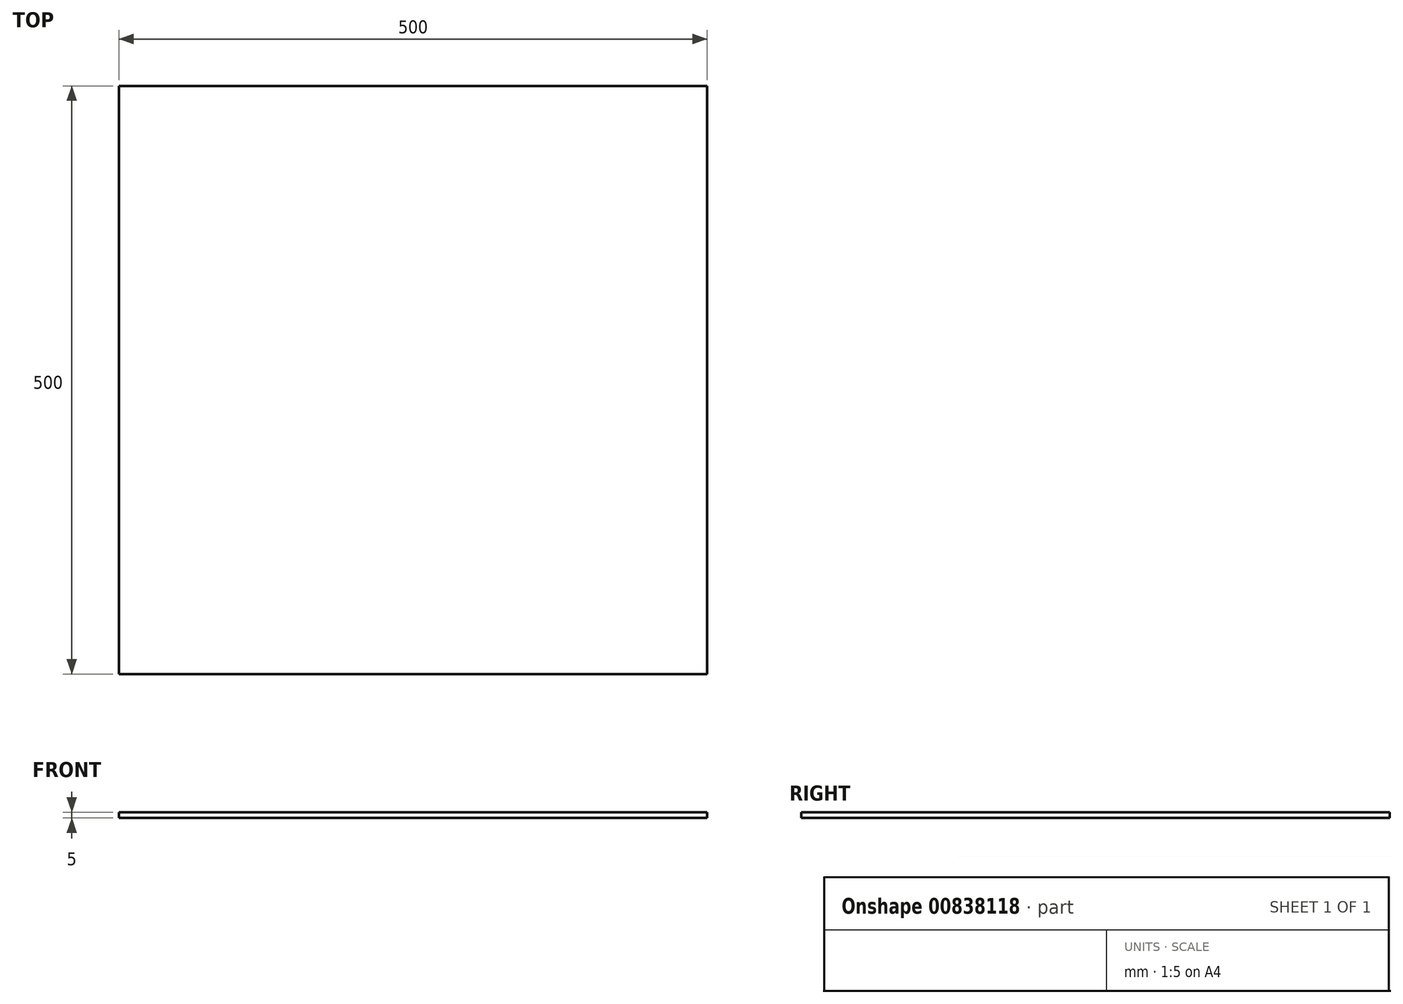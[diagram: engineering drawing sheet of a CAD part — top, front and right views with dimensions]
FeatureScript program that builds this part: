
annotation { "Feature Type Name" : "Feature", "Feature Type Description" : "" }
export const myFeature = defineFeature(function(context is Context, id is Id, definition is map)
    precondition{}
    {
        {
            var Q0;
            Q0=qCreatedBy(makeId("Top.planeOp"),FACE);
            var sketch = newSketch(context, id + "F0", { "sketchPlane" : qUnion([Q0])});
            skLineSegment(sketch, "E0.bottom", {"start": v(250, -250) * mm, "end": v(-250, -250) * mm});
            skLineSegment(sketch, "E0.top", {"start": v(250, 250) * mm, "end": v(-250, 250) * mm});
            skLineSegment(sketch, "E0.left", {"start": v(250, -250) * mm, "end": v(250, 250) * mm});
            skLineSegment(sketch, "E0.right", {"start": v(-250, -250) * mm, "end": v(-250, 250) * mm});
            skPoint(sketch, "E0.middle", {"position": v(0, 0) * mm});
            skSolve(sketch);
        }
        {
            var Q0;
            Q0=makeQuery(id+"F0.imprint","IMPRINT",FACE,{"disambiguationData":[TD([[makeQuery(id+"F0.imprint","IMPRINT",EDGE,{"derivedFrom":sQuery(id+"F0.wireOp",EDGE,"E0.bottom")}),-1.0]])]});
            extrude(context, id + "F1", {"entities" : qUnion([Q0]), "depth" : 5 * mm, "offsetDistance" : 25 * mm});
        }
    });
